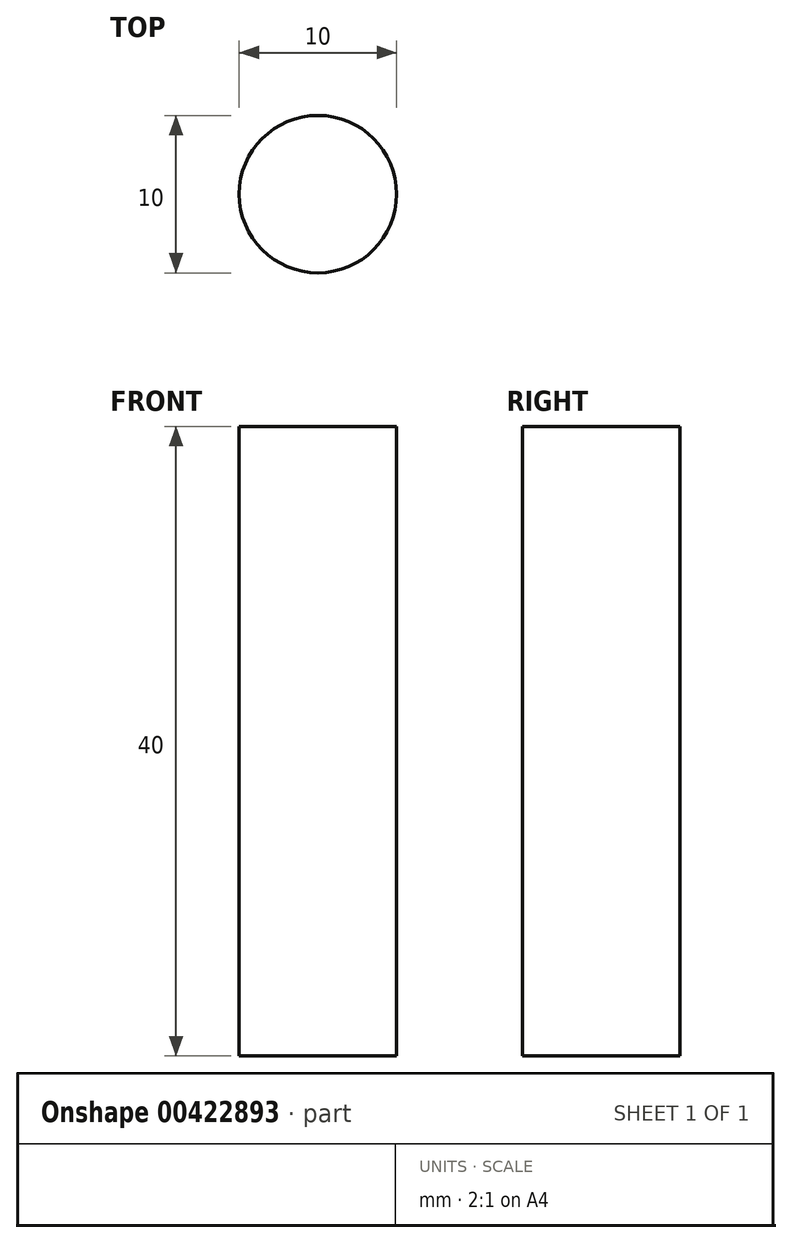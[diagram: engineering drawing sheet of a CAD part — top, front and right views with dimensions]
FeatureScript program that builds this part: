
annotation { "Feature Type Name" : "Feature", "Feature Type Description" : "" }
export const myFeature = defineFeature(function(context is Context, id is Id, definition is map)
    precondition{}
    {
        {
            var Q0;
            Q0=qCreatedBy(makeId("Front.planeOp"),FACE);
            var sketch = newSketch(context, id + "F0", { "sketchPlane" : qUnion([Q0])});
            skLineSegment(sketch, "E0.bottom", {"start": v(0, 0) * mm, "end": v(5, 0) * mm});
            skLineSegment(sketch, "E0.top", {"start": v(0, 40) * mm, "end": v(5, 40) * mm});
            skLineSegment(sketch, "E0.left", {"start": v(0, 0) * mm, "end": v(0, 40) * mm});
            skLineSegment(sketch, "E0.right", {"start": v(5, 0) * mm, "end": v(5, 40) * mm});
            skSolve(sketch);
        }
        {
            var Q0;
            Q0=makeQuery(id+"F0.imprint","IMPRINT",FACE,{"disambiguationData":[TD([[makeQuery(id+"F0.imprint","IMPRINT",EDGE,{"derivedFrom":sQuery(id+"F0.wireOp",EDGE,"E0.bottom")}),1.0]])]});
            var Q1;
            Q1=sQuery(id+"F0.wireOp",EDGE,"E0.left");
            revolve(context, id + "F1", {"entities" : qUnion([Q0]), "axis" : qUnion([Q1]), "revolveType" : RevolveType.FULL});
        }
    });
